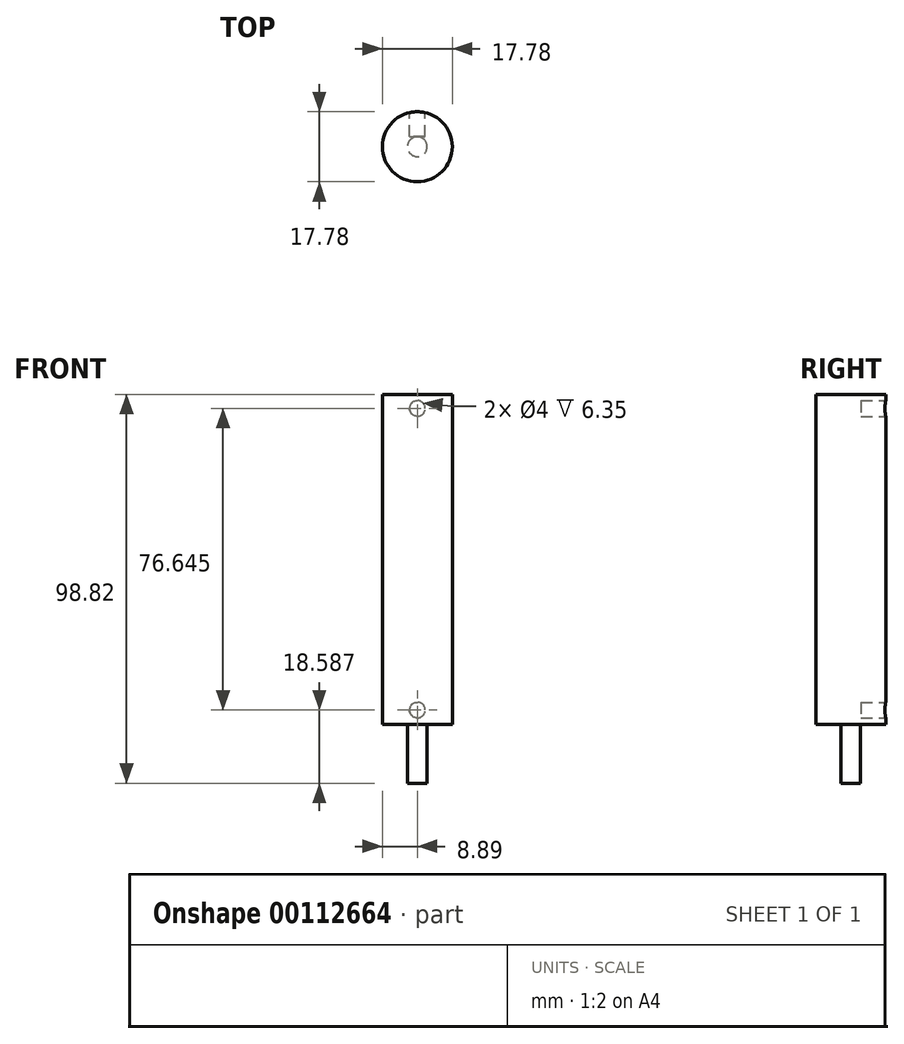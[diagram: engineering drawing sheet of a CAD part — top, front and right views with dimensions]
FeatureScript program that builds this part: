
annotation { "Feature Type Name" : "Feature", "Feature Type Description" : "" }
export const myFeature = defineFeature(function(context is Context, id is Id, definition is map)
    precondition{}
    {
        {
            var Q0;
            Q0=qCreatedBy(makeId("Top.planeOp"),FACE);
            var sketch = newSketch(context, id + "F0", { "sketchPlane" : qUnion([Q0])});
            skCircle(sketch, "E0", {"center": v(0, 0) * mm, "radius": 8.9 * mm, "construction": true});
            skLineSegment(sketch, "E1.bottom", {"start": v(8.9, 8.89) * mm, "end": v(-8.89, 8.89) * mm});
            skLineSegment(sketch, "E1.top", {"start": v(8.9, -8.89) * mm, "end": v(-8.89, -8.89) * mm});
            skLineSegment(sketch, "E1.left", {"start": v(8.9, 8.89) * mm, "end": v(8.9, -8.89) * mm});
            skLineSegment(sketch, "E1.right", {"start": v(-8.89, 8.89) * mm, "end": v(-8.89, -8.89) * mm});
            skSolve(sketch);
        }
        {
            var Q0;
            Q0 = qSketchRegion(id + "F0", true);
            extrude(context, id + "F1", {"entities" : qUnion([Q0]), "depth" : 83.82 * mm});
        }
        {
            var Q0;
            Q0=makeQuery(id+"F1.opExtrude","CAP_FACE",FACE,{"disambiguationData":[OSD([sQuery(id+"F0.wireOp",EDGE,"E1.bottom"),sQuery(id+"F0.wireOp",EDGE,"E1.top"),sQuery(id+"F0.wireOp",EDGE,"E1.left"),sQuery(id+"F0.wireOp",EDGE,"E1.right")])],"isStart":true});
            var sketch = newSketch(context, id + "F2", { "sketchPlane" : qUnion([Q0])});
            skCircle(sketch, "E2", {"center": v(0, 0) * mm, "radius": 2.5 * mm});
            skSolve(sketch);
        }
        {
            var Q0;
            Q0 = qSketchRegion(id + "F2", true);
            extrude(context, id + "F3", {"entities" : qUnion([Q0]), "operationType" : NewBodyOperationType.ADD, "depth" : 15 * mm});
        }
        {
            var Q0;
            Q0=makeQuery(id+"F1.opExtrude","SWEPT_FACE",FACE,{"disambiguationData":[OSD([sQuery(id+"F0.wireOp",EDGE,"E1.bottom")])]});
            var sketch = newSketch(context, id + "F4", { "sketchPlane" : qUnion([Q0])});
            skLineSegment(sketch, "E3", {"start": v(0, 83.82) * mm, "end": v(0, 80.23) * mm, "construction": true});
            skLineSegment(sketch, "E4", {"start": v(0, 0) * mm, "end": v(0, 3.59) * mm, "construction": true});
            skCircle(sketch, "E5", {"center": v(0, 3.59) * mm, "radius": 2 * mm});
            skCircle(sketch, "E6", {"center": v(0, 80.23) * mm, "radius": 2 * mm});
            skSolve(sketch);
        }
        {
            var Q0;
            Q0 = qSketchRegion(id + "F4", true);
            extrude(context, id + "F5", {"entities" : qUnion([Q0]), "operationType" : NewBodyOperationType.REMOVE, "oppositeDirection" : true, "depth" : 6.35 * mm});
        }
        {
            var Q0;
            Q0=makeQuery(id+"F1.opExtrude","SWEPT_EDGE",EDGE,{"disambiguationData":[OSD([sQuery(id+"F0.wireOp",EDGE,"E1.top"),sQuery(id+"F0.wireOp",EDGE,"E1.left")])]});
            var Q1;
            Q1=makeQuery(id+"F1.opExtrude","SWEPT_EDGE",EDGE,{"disambiguationData":[OSD([sQuery(id+"F0.wireOp",EDGE,"E1.bottom"),sQuery(id+"F0.wireOp",EDGE,"E1.left")])]});
            var Q2;
            Q2=makeQuery(id+"F1.opExtrude","SWEPT_EDGE",EDGE,{"disambiguationData":[OSD([sQuery(id+"F0.wireOp",EDGE,"E1.bottom"),sQuery(id+"F0.wireOp",EDGE,"E1.right")])]});
            var Q3;
            Q3=makeQuery(id+"F1.opExtrude","SWEPT_EDGE",EDGE,{"disambiguationData":[OSD([sQuery(id+"F0.wireOp",EDGE,"E1.top"),sQuery(id+"F0.wireOp",EDGE,"E1.right")])]});
            fillet(context, id + "F6", {"entities" : qUnion([Q0, Q1, Q2, Q3]), "radius" : 8.9 * mm, "tangentPropagation" : true, "allowEdgeOverflow" : false});
        }
    });
